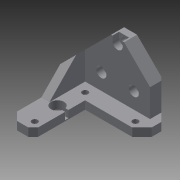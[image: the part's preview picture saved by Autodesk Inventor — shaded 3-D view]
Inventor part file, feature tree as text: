
AUTODESK INVENTOR PART (.ipt)
format: ipt  version: 2015 SP2 (Build 190223200, 223)  size: 219,136 bytes
history: native  units: mm
features: sketch x10, extrude x7, chamfer x4, hole x3
ambient origin geometry x8: Origin, YZ Plane, XZ Plane, XY Plane, X Axis, Y Axis, Z Axis, Center Point
bodies: Solid1 (feature_tree)
feature tree (24):
  extrude  "Extrusion1"  Depth=50.0mm
  extrude  "Extrusion2"  Depth=15.0mm
  extrude  "Extrusion3"  Depth=38.0mm TaperAngle=0.0deg
  extrude  "Extrusion4"  Depth=5.0mm
  extrude  "Extrusion5"  TaperAngle=0.0deg  [1 undecoded]
  chamfer  "Chamfer1"  Distance=17.0mm
  chamfer  "Chamfer2"  Distance=33.0mm
  chamfer  "Chamfer3"  [1 undecoded]
  chamfer  "Chamfer4"  Distance=17.0mm
  hole  "Hole1"  [1 undecoded]
  hole  "Hole2"  [1 undecoded]
  hole  "Hole3"  [1 undecoded]
  extrude  "Extrusion6"  TaperAngle=0.0deg  [1 undecoded]
  extrude  "Extrusion7"  Depth=5.0mm TaperAngle=45.0deg
  sketch  "Sketch2"  dims[d0=50.0mm d1=50.0mm]
  sketch  "Sketch3"  dims[d2=38.0mm d3=0.0mm d4=15.0mm]
  sketch  "Sketch4"  dims[d5=18.0mm d6=38.0mm d7=0.0mm]
  sketch  "Sketch6"  dims[d8=8.0mm d9=5.0mm]
  sketch  "Sketch8"  dims[d10=33.0mm d11=0.0mm]
  sketch  "Sketch9"  dims[d12=8.0mm]
  sketch  "Sketch10"  dims[d13=5.0mm]
  sketch  "Sketch11"  dims[d14=5.0mm]
  sketch  "Sketch12"  dims[d15=135.0deg]
  sketch  "Sketch13"  dims[d16=135.0deg d17=17.0mm d18=33.0mm d19=0.0mm d20=17.0mm d21=5.5mm d22=20.0mm d23=33.0mm d24=0.0mm d25=5.0mm d26=5.0mm d27=45.0deg d28=3.0mm d29=3.0mm d30=45.0deg d31=6.0mm d32=6.0mm d33=45.0deg d34=6.0mm d35=6.0mm d36=45.0deg d37=20.0mm d38=10.0mm d39=20.0mm d40=3.0mm d41=3.6mm d42=6.0mm d43=6.2mm d44=4.0mm d45=90.0deg d46=8.0mm d47=20.594885mm d48=4.2mm d49=4.2mm d50=31.0mm d51=31.0mm d52=3.6mm d53=6.0mm d54=4.0mm d55=2.0mm d56=90.0deg d57=8.0mm d58=20.594885mm d60=20.7mm d61=8.0mm d62=6.0mm d63=4.0mm d64=2.0mm d65=90.0deg d66=8.0mm d67=20.594885mm d68=20.7mm d69=0.6mm d70=2.0mm d71=10.0mm d72=0.0mm d73=6.2mm d74=4.0mm d75=10.0mm d76=0.0mm d77=4.3mm]
note: 6 required parameter values undecoded (feature->parameter linkage not recoverable at this tier; creation-order binding heuristic only, values carry confidence <= 0.55)
